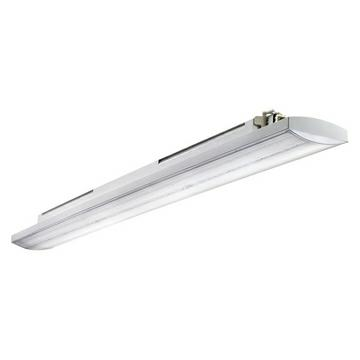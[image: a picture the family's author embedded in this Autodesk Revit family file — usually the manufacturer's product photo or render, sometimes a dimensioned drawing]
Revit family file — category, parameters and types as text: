
# Revit family: Lighting-Industrial-GEWISS-SMART[3]PLUS-HLO-WATERTIGHT-LED-EMERGENCY_TRANSPARENT_1600mm
name_source: partatom
category: Apparecchi per illuminazione
units: mm (PartAtom-declared; Revit-internal decimal feet)

## family parameters
Condiviso = No
Host = Superficie
Punto di calcolo locali = No
Quota connettore circolare = Usa diametro
Sorgente d'illuminazione = No
Taglio con vuoti quando caricato = No
Tipo di parte = Normale

## types (1)
- Lighting-Industrial-GEWISS-SMART[3]PLUS-HLO-WATERTIGHT-LED-EMERGENCY_TRANSPARENT_1600mm
    Application = Indoor
    Carico apparente = 26 VA
    Catalogue = LIGHTING
    Catalogue Range = SMART[3] PLUS HLO
    Colour temperature = 5700 K (CRI > 90)
    Colour temperature: = 5700 K (CRI > 90)
    Commenti sul wattaggio = 26W
    Descrizione = SMART3 PLUS 1600 EMERG DT1+DT6 HO TRASP 9 57
    Efficiency class of integrated LEDs = A ÷ A++
    Electrocod = 2434
    Ganci = Alluminio
    Glow Wire Test = 850°C
    IDF = d46191a8-45a4-4aa7-8cad-d7a8957d08f7
    IDT = 0d0c36dd-7d20-424d-bc0a-e9538265b617
    IP degree = IP66/IP69
    Immagine tipo = GWS3158TL.jpg
    Insulation class = II
    Lamp = LED
    Lampada = LED
    Length = 1600 mm
    Lumen output (lm) = 7400
    Lunghezza Lampada = 1600 mm
    Modello = GWS3325BT957
    Numero poli = 2
    Operating temperature: = ND
    Produttore = GEWISS S.p.A.
    Prospetto di default = 1219 mm
    SEO = Ceiling
    Schermo. = Led Acceso
    Shield type = Transparent
    Shock resistance = IK08
    Stampa 1_100 = Sì
    Stampa 1_200 = No
    Struttura = GRIGIO
    System power = 50 W
    Technical sheet = https://www.gewiss.com
    Type of light source = LED - Not replaceable
    URL = https://www.gewiss.com
    Version file RFA = 20.0
    Voltage = 220-240 V
    Warranty = ND
    Working temperature = ND
